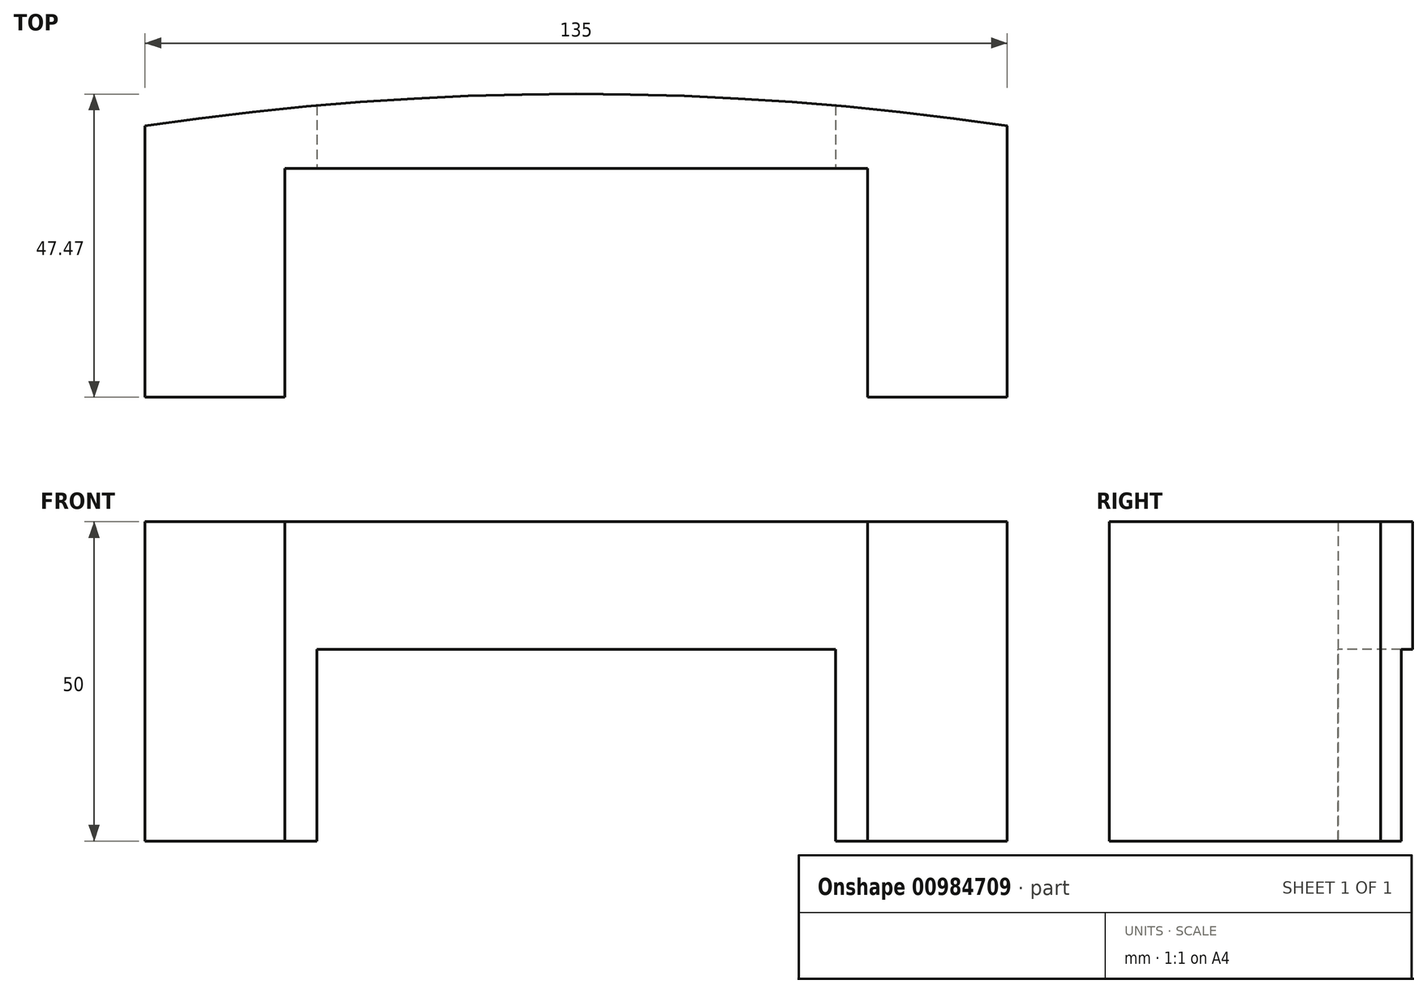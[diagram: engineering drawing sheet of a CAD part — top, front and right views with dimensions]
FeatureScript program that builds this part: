
annotation { "Feature Type Name" : "Feature", "Feature Type Description" : "" }
export const myFeature = defineFeature(function(context is Context, id is Id, definition is map)
    precondition{}
    {
        {
            var Q0;
            Q0=qCreatedBy(makeId("Top.planeOp"),FACE);
            var sketch = newSketch(context, id + "F0", { "sketchPlane" : qUnion([Q0])});
            skLineSegment(sketch, "E0", {"start": v(0, 20.7) * mm, "end": v(-67.5, 20.7) * mm, "construction": true});
            skLineSegment(sketch, "E1", {"start": v(-67.5, 20.7) * mm, "end": v(-67.5, -21.77) * mm});
            skLineSegment(sketch, "E2", {"start": v(-67.5, -21.77) * mm, "end": v(-45.62, -21.77) * mm});
            skLineSegment(sketch, "E3", {"start": v(-45.62, -21.77) * mm, "end": v(-45.62, 14.03) * mm});
            skLineSegment(sketch, "E4", {"start": v(-45.62, 14.03) * mm, "end": v(0, 14.03) * mm});
            skLineSegment(sketch, "E5", {"start": v(0, 14.03) * mm, "end": v(0, 20.7) * mm, "construction": true});
            skLineSegment(sketch, "E6.MirrorCS", {"start": v(45.62, 14.03) * mm, "end": v(0, 14.03) * mm});
            skLineSegment(sketch, "E7.MirrorCS", {"start": v(0, 20.7) * mm, "end": v(67.5, 20.7) * mm, "construction": true});
            skLineSegment(sketch, "E8.MirrorCS", {"start": v(67.5, 20.7) * mm, "end": v(67.5, -21.77) * mm});
            skLineSegment(sketch, "E9.MirrorCS", {"start": v(67.5, -21.77) * mm, "end": v(45.62, -21.77) * mm});
            skLineSegment(sketch, "E10.MirrorCS", {"start": v(45.62, -21.77) * mm, "end": v(45.62, 14.03) * mm});
            skArc(sketch, "E11", {"start": v(67.5, 20.7) * mm, "mid": v(0, 25.7) * mm, "end": v(-67.5, 20.7) * mm});
            skPoint(sketch, "E12", {"position": v(0, 25.7) * mm});
            skSolve(sketch);
        }
        {
            var Q0;
            Q0 = qSketchRegion(id + "F0", true);
            extrude(context, id + "F1", {"entities" : qUnion([Q0]), "depth" : 50 * mm, "offsetDistance" : 25 * mm});
        }
        {
            var Q0;
            Q0=qCreatedBy(makeId("Front.planeOp"),FACE);
            var sketch = newSketch(context, id + "F2", { "sketchPlane" : qUnion([Q0])});
            skLineSegment(sketch, "E13.bottom", {"start": v(40.62, 30) * mm, "end": v(-40.62, 30) * mm});
            skLineSegment(sketch, "E13.top", {"start": v(40.62, -7.2) * mm, "end": v(-40.62, -7.2) * mm});
            skLineSegment(sketch, "E13.left", {"start": v(40.62, 30) * mm, "end": v(40.62, -7.2) * mm});
            skLineSegment(sketch, "E13.right", {"start": v(-40.62, 30) * mm, "end": v(-40.62, -7.2) * mm});
            skSolve(sketch);
        }
        {
            var Q0;
            Q0 = qSketchRegion(id + "F2", true);
            extrude(context, id + "F3", {"entities" : qUnion([Q0]), "operationType" : NewBodyOperationType.REMOVE, "oppositeDirection" : true, "depth" : 30 * mm, "offsetDistance" : 25 * mm});
        }
    });
